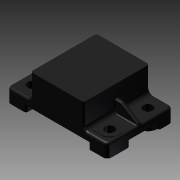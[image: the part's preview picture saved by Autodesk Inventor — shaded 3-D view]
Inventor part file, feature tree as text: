
AUTODESK INVENTOR PART (.ipt)
format: ipt  version: 2013 (Build 170138000, 138)  size: 427,008 bytes
history: native  units: mm (DEFAULTED — no unit token found)
features: sketch x12, extrude x11, fillet x5, mirror x3, plane x2, rib x1
ambient origin geometry x8: Origin, YZ Plane, XZ Plane, XY Plane, X Axis, Y Axis, Z Axis, Center Point
bodies: Solid1 (feature_tree)
feature tree (34):
  extrude  "Extrusion1"  Depth=5.08mm
  fillet  "Fillet19"  Radius=73.66mm
  extrude  "Extrusion4"  Depth=48.26mm TaperAngle=0.0deg
  fillet  "Fillet20"  Radius=3.048mm
  extrude  "Extrusion10"  Depth=1.524mm
  extrude  "Extrusion12"  Depth=10.16mm
  fillet  "Fillet21"  Radius=8.255mm
  plane  "Work Plane3"
  plane  "Work Plane4"
  mirror  "Mirror4"
  mirror  "Mirror5"
  extrude  "Extrusion11"  Depth=0.381mm TaperAngle=0.0deg
  extrude  "Extrusion13"  Depth=3.302mm
  extrude  "Extrusion14"  Depth=8.636mm
  extrude  "Extrusion15"  Depth=2.54mm
  extrude  "Extrusion16"  Depth=0.762mm
  extrude  "Extrusion5"  Depth=3.048mm
  extrude  "Extrusion6"  Depth=13.97mm
  rib  "Rib2"
  fillet  "Fillet22"  Radius=16.51mm
  fillet  "Fillet23"  Radius=4.826mm
  mirror  "Mirror6"
  sketch  "Sketch1"  dims[d1=23.099032mm d2=5.08mm d3=73.66mm]
  sketch  "Sketch5"  dims[d4=38.862mm d5=48.26mm d6=0.0mm d40=3.048mm]
  sketch  "Sketch6"  dims[d41=3.048mm d42=1.524mm]
  sketch  "Sketch7"  dims[d43=6.858mm d44=10.16mm d45=8.255mm]
  sketch  "Sketch8"  dims[d46=8.89mm d47=0.0mm d48=0.381mm d49=0.0mm]
  sketch  "Sketch14"  dims[d50=0.381mm d51=0.0mm d52=3.302mm]
  sketch  "Sketch15"  dims[d53=3.302mm d54=8.636mm]
  sketch  "Sketch16"  dims[d55=3.302mm d56=2.54mm]
  sketch  "Sketch17"  dims[d57=2.54mm d58=0.762mm]
  sketch  "Sketch18"  dims[d59=0.762mm d83=3.048mm]
  sketch  "Sketch19"  dims[d84=1.524mm d85=13.97mm d86=16.51mm d87=4.826mm d88=0.0mm]
  sketch  "Sketch20"  dims[d89=1.27mm d90=4.826mm d91=0.0mm d92=3.048mm d93=1.524mm d94=16.51mm d95=13.97mm d96=4.826mm d97=0.0mm d98=1.27mm d99=4.826mm d100=0.0mm d101=13.97mm d102=13.97mm d103=3.048mm d104=1.524mm d105=1.016mm d106=3.048mm d107=1.524mm d108=1.016mm d109=13.97mm d110=4.826mm d111=0.0mm d112=1.27mm d113=1.27mm d114=0.381mm d116=0.381mm d117=13.97mm d118=4.826mm d119=0.0mm d120=1.27mm d121=0.381mm d122=0.381mm d124=13.97mm d125=4.826mm d126=0.0mm]
